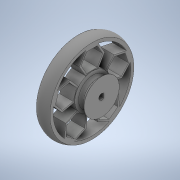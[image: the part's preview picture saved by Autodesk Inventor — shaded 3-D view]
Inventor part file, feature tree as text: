
AUTODESK INVENTOR PART (.ipt)
format: ipt  version: 2020 (Build 240168000, 168)  size: 438,784 bytes
history: native  units: in
note: dims shown in document units (in); Inventor stores cm internally (conversion verified against a paired STEP export)
features: sketch x4, extrude x2, revolve x2, projected_geometry x1
ambient origin geometry x8: Origin, YZ Plane, XZ Plane, XY Plane, X Axis, Y Axis, Z Axis, Center Point
bodies: Solid1 (feature_tree)
feature tree (9):
  extrude  "Extrusion1"  Depth=0.0394in
  sketch  "Sketch3"  dims[d6=0.7087in d7=0.1969in]
  revolve  "Revolution1"  [1 undecoded]
  extrude  "Extrusion2"  Depth=0.1969in
  revolve  "Revolution2"  [1 undecoded]
  sketch  "Sketch1"  dims[d0=0.1181in d1=0.0394in]
  sketch  "Sketch2"  dims[d3=1.6929in d4=0.1181in]
  projected_geometry  "Projected Loop1"
  sketch  "Sketch4"  dims[d8=0.0in d9=1.6929in d10=0.063in d11=0.0315in d16=0.2756in d17=0.0in d19=360.0deg d20=0.0984in d24=0.0394in d25=90.0deg d26=45.0deg d28=0.0079in d29=1.9685in d31=360.0deg]
note: 2 required parameter values undecoded (feature->parameter linkage not recoverable at this tier; creation-order binding heuristic only, values carry confidence <= 0.55)
